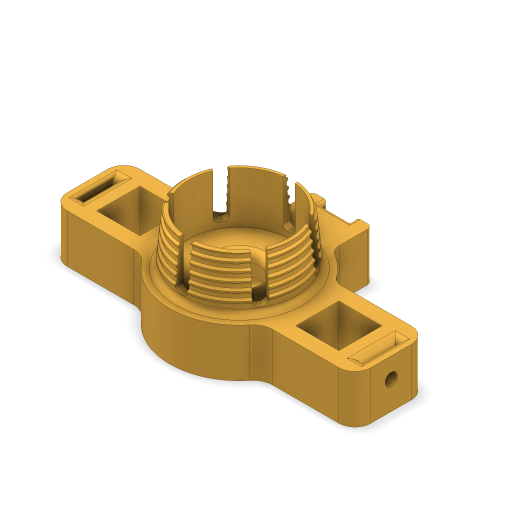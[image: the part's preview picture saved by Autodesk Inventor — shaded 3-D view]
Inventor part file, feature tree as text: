
AUTODESK INVENTOR PART (.ipt)
format: ipt  version: 2023 (Build 270158000, 158)  size: 1,398,784 bytes
history: native  units: mm
features: fillet x11, sketch x7, extrude x5, hole x3, helix x2, direct_edit x2, draft x1, plane x1, mirror x1, other x1, revolve x1
ambient origin geometry x8: Origin, YZ Plane, XZ Plane, XY Plane, X Axis, Y Axis, Z Axis, Center Point
bodies: Solid1 (feature_tree)
feature tree (35):
  extrude  "Extrusion1"  Depth=26.5mm
  draft  "FaceDraft1"
  sketch  "Sketch2"  dims[d34=0.0mm d35=0.0mm d56=8.726646mm]
  helix  "Coil3"  [1 undecoded]
  helix  "Coil4"  [1 undecoded]
  direct_edit  "Direct Edit2"
  extrude  "Extrusion2"  Depth=8.726646mm
  extrude  "Extrusion13"  TaperAngle=90.0deg  [1 undecoded]
  plane  "Work Plane5"
  extrude  "Extrusion14"  Depth=34.58632mm
  hole  "Hole3"  [1 undecoded]
  hole  "Hole4"  [1 undecoded]
  fillet  "Fillet11"  Radius=60.0mm
  fillet  "Fillet22"  [1 undecoded]
  hole  "Hole6"  [1 undecoded]
  mirror  "Mirror3"
  extrude  "Extrusion15"  Depth=1.2mm
  direct_edit  "Direct Edit3"
  fillet  "Fillet23"  Radius=18.0mm
  fillet  "Fillet13"  Radius=10.7mm
  fillet  "Fillet15"  Radius=10.0mm
  fillet  "Fillet16"  Radius=15.0mm
  fillet  "Fillet17"  Radius=10.0mm
  fillet  "Fillet18"  Radius=7.0mm
  fillet  "Fillet19"  Radius=10.0mm
  fillet  "Fillet20"  Radius=1.0mm
  fillet  "Fillet21"  [1 undecoded]
  sketch  "Sketch1"  dims[d0=25.0mm d1=26.5mm d2=12.875mm d3=0.0mm d4=1.047198mm]
  sketch  "Sketch3"  dims[d62=2.0mm d63=10.15mm d64=10.0mm d65=1.047198mm]
  sketch  "Sketch13"  dims[d66=90.0deg d67=90.0deg d68=0.0mm d69=0.0mm d70=2.0mm d71=3.0mm d72=10.0mm d73=-1.047198mm d74=90.0deg d75=90.0deg d76=0.0mm d77=0.0mm]
  sketch  "Sketch14"  dims[d79=-0.127mm d145=34.58632mm]
  sketch  "Sketch16"  dims[d150=120.0deg d151=120.0deg]
  sketch  "Sketch17"  dims[d153=21.6866mm d157=12.0mm d158=0.0mm d160=60.0mm d162=360.0deg d164=0.0mm d165=0.0mm d179=5.3mm d180=6.0mm d181=4.0mm d182=2.0mm d183=90.0deg d184=5.0mm d185=0.0mm d186=10.0mm d187=6.0mm d188=4.0mm d189=2.0mm d190=90.0deg d191=7.0mm d192=0.0mm d193=2.0mm d194=20.0mm d195=18.0mm d196=10.7mm d197=10.0mm d206=15.0mm d207=10.0mm d208=7.0mm d209=10.0mm d210=1.0mm d211=0.0mm d212=-4.363323mm d213=1.0mm d215=1.5mm d216=3.0mm d217=8.0mm d219=1.0mm d220=5.0mm d221=3.0mm d222=6.0mm d223=4.0mm d224=2.0mm d225=90.0deg d226=6.5mm d227=0.0mm d228=3.0mm d229=5.0mm d230=4.0mm d234=2.0mm d235=0.7mm d237=1.5mm d238=1.2mm d239=1.3mm d240=1.2mm d109=0.5mm d110=0.872665mm d111=0.5mm d112=0.872665mm d236=0.5mm]
  other  "Size2"
  revolve  "Rotate1"  [1 undecoded]
note: 9 required parameter values undecoded (feature->parameter linkage not recoverable at this tier; creation-order binding heuristic only, values carry confidence <= 0.55)